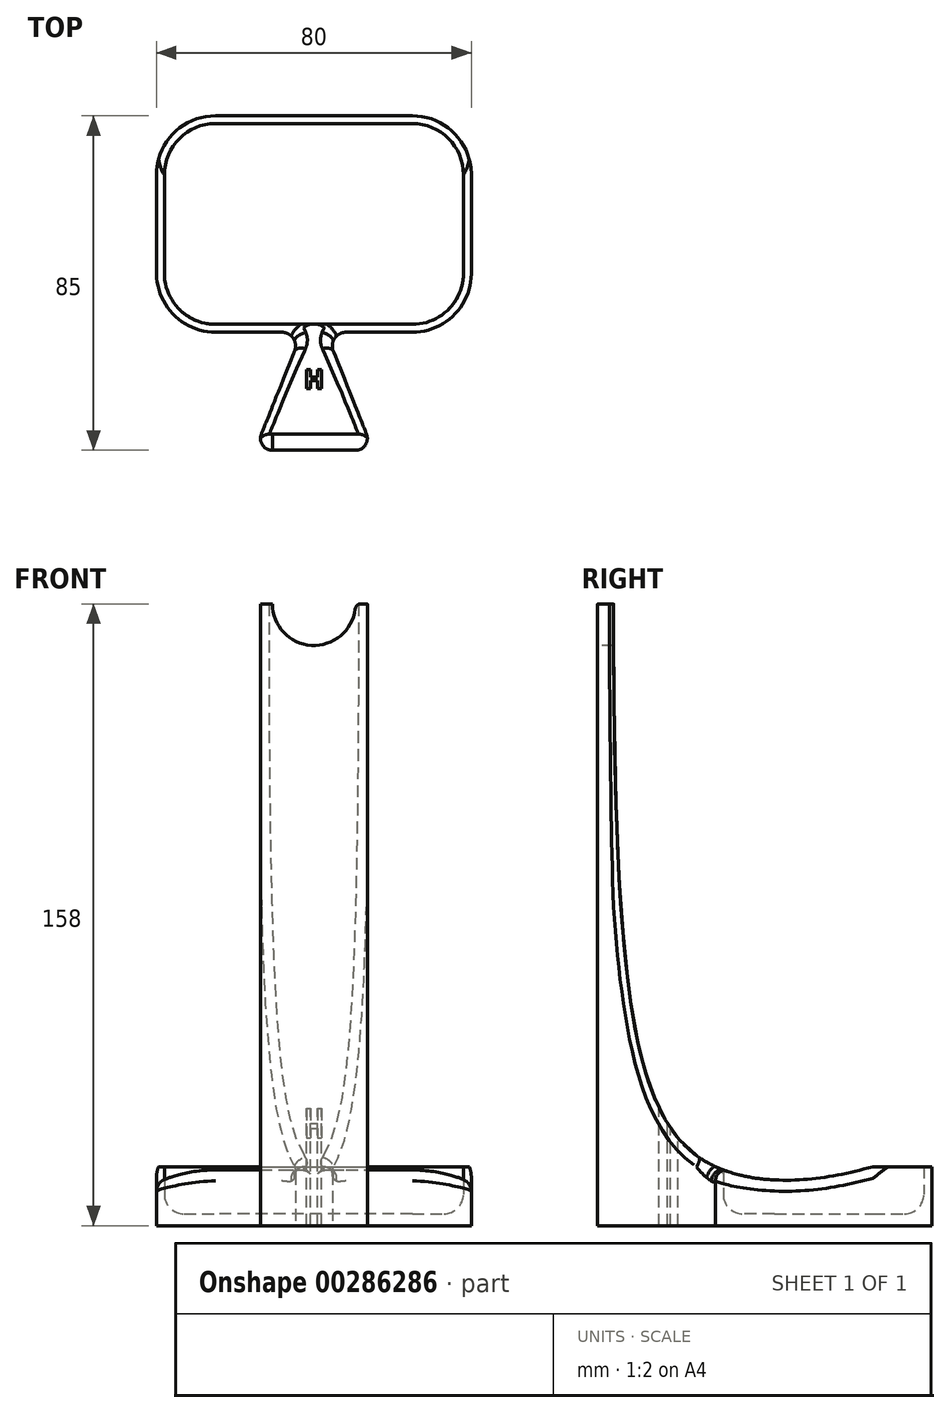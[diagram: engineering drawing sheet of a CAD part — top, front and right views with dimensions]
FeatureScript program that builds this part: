
annotation { "Feature Type Name" : "Feature", "Feature Type Description" : "" }
export const myFeature = defineFeature(function(context is Context, id is Id, definition is map)
    precondition{}
    {
        {
            var Q0;
            Q0=qCreatedBy(makeId("Top.planeOp"),FACE);
            var sketch = newSketch(context, id + "F0", { "sketchPlane" : qUnion([Q0])});
            skLineSegment(sketch, "E0.bottom", {"start": v(-25, 27.5) * mm, "end": v(25, 27.5) * mm});
            skLineSegment(sketch, "E0.top", {"start": v(-25, -27.5) * mm, "end": v(25, -27.5) * mm});
            skLineSegment(sketch, "E0.left", {"start": v(-40, 12.5) * mm, "end": v(-40, -12.5) * mm});
            skLineSegment(sketch, "E0.right", {"start": v(40, 12.5) * mm, "end": v(40, -12.5) * mm});
            skPoint(sketch, "E0.middle", {"position": v(0, 0) * mm});
            skPoint(sketch, "E1.visualSharp", {"position": v(-40, 27.5) * mm});
            skArc(sketch, "E1.filletArc", {"start": v(-25, 27.5) * mm, "mid": v(-35.6, 23.1) * mm, "end": v(-40, 12.5) * mm});
            skPoint(sketch, "E2.visualSharp", {"position": v(40, 27.5) * mm});
            skArc(sketch, "E2.filletArc", {"start": v(40, 12.5) * mm, "mid": v(35.6, 23.1) * mm, "end": v(25, 27.5) * mm});
            skPoint(sketch, "E3.visualSharp", {"position": v(40, -27.5) * mm});
            skArc(sketch, "E3.filletArc", {"start": v(25, -27.5) * mm, "mid": v(35.6, -23.1) * mm, "end": v(40, -12.5) * mm});
            skPoint(sketch, "E4.visualSharp", {"position": v(-40, -27.5) * mm});
            skArc(sketch, "E4.filletArc", {"start": v(-40, -12.5) * mm, "mid": v(-35.6, -23.1) * mm, "end": v(-25, -27.5) * mm});
            skArc(sketch, "E5.0", {"start": v(-25, 25.5) * mm, "mid": v(-34.2, 21.7) * mm, "end": v(-38, 12.5) * mm});
            skLineSegment(sketch, "E5.1", {"start": v(-38, 12.5) * mm, "end": v(-38, -12.5) * mm});
            skLineSegment(sketch, "E5.2", {"start": v(-25, 25.5) * mm, "end": v(25, 25.5) * mm});
            skArc(sketch, "E5.3", {"start": v(-38, -12.5) * mm, "mid": v(-34.2, -21.7) * mm, "end": v(-25, -25.5) * mm});
            skArc(sketch, "E5.4", {"start": v(38, 12.5) * mm, "mid": v(34.2, 21.7) * mm, "end": v(25, 25.5) * mm});
            skLineSegment(sketch, "E5.5", {"start": v(38, 12.5) * mm, "end": v(38, -12.5) * mm});
            skArc(sketch, "E5.6", {"start": v(25, -25.5) * mm, "mid": v(34.2, -21.7) * mm, "end": v(38, -12.5) * mm});
            skLineSegment(sketch, "E5.7", {"start": v(-25, -25.5) * mm, "end": v(25, -25.5) * mm});
            skLineSegment(sketch, "E6", {"start": v(-4.92, -32.3) * mm, "end": v(-13.35, -53.39) * mm});
            skLineSegment(sketch, "E7", {"start": v(-10.57, -57.5) * mm, "end": v(10.57, -57.5) * mm});
            skLineSegment(sketch, "E8", {"start": v(13.35, -53.39) * mm, "end": v(4.92, -32.3) * mm});
            skPoint(sketch, "E9", {"position": v(0, -57.5) * mm});
            skArc(sketch, "E10", {"start": v(-4.92, -32.3) * mm, "mid": v(-5.27, -29.04) * mm, "end": v(-8.17, -27.5) * mm});
            skArc(sketch, "E11.MirrorC", {"start": v(4.92, -32.3) * mm, "mid": v(5.27, -29.04) * mm, "end": v(8.17, -27.5) * mm});
            skPoint(sketch, "E12.orphan", {"position": v(3, -27.5) * mm});
            skPoint(sketch, "E13.orphan", {"position": v(-3, -27.5) * mm});
            skPoint(sketch, "E14.visualSharp", {"position": v(-15, -57.5) * mm});
            skArc(sketch, "E14.filletArc", {"start": v(-13.35, -53.39) * mm, "mid": v(-13.05, -56.18) * mm, "end": v(-10.57, -57.5) * mm});
            skPoint(sketch, "E15.visualSharp", {"position": v(15, -57.5) * mm});
            skArc(sketch, "E15.filletArc", {"start": v(10.57, -57.5) * mm, "mid": v(13.05, -56.18) * mm, "end": v(13.35, -53.39) * mm});
            skSolve(sketch);
        }
        {
            var Q0;
            Q0=makeQuery(id+"F0.imprint","IMPRINT",FACE,{"disambiguationData":[TD([[makeQuery(id+"F0.imprint","IMPRINT",EDGE,{"derivedFrom":sQuery(id+"F0.wireOp",EDGE,"E0.bottom")}),-1.0]])]});
            var Q1;
            Q1=makeQuery(id+"F0.imprint","IMPRINT",FACE,{"disambiguationData":[TD([[makeQuery(id+"F0.imprint","IMPRINT",EDGE,{"derivedFrom":sQuery(id+"F0.wireOp",EDGE,"E5.0")}),1.0]])]});
            var Q2;
            {var subQ0=sQuery(id+"F0.wireOp",EDGE,"E6");Q2=makeQuery(id+"F0.imprint","IMPRINT",FACE,{"disambiguationData":[TD([[makeQuery(id+"F0.imprint","IMPRINT",EDGE,{"derivedFrom":subQ0}),1.0]])]});}
            extrude(context, id + "F1", {"entities" : qUnion([Q0, Q1, Q2]), "depth" : 3 * mm});
        }
        {
            var Q0;
            Q0=makeQuery(id+"F0.imprint","IMPRINT",FACE,{"disambiguationData":[TD([[makeQuery(id+"F0.imprint","IMPRINT",EDGE,{"derivedFrom":sQuery(id+"F0.wireOp",EDGE,"E0.bottom")}),-1.0]])]});
            extrude(context, id + "F2", {"entities" : qUnion([Q0]), "operationType" : NewBodyOperationType.ADD, "depth" : 15 * mm});
        }
        {
            var Q0;
            {var subQ0=sQuery(id+"F0.wireOp",EDGE,"E7");var subQ1=sQuery(id+"F0.wireOp",EDGE,"E6");var subQ2=sQuery(id+"F0.wireOp",EDGE,"E3.filletArc");var subQ3=sQuery(id+"F0.wireOp",EDGE,"E0.top");var subQ4=sQuery(id+"F0.wireOp",EDGE,"E11.MirrorC");var subQ5=sQuery(id+"F0.wireOp",EDGE,"E4.filletArc");var subQ6=sQuery(id+"F0.wireOp",EDGE,"E10");var subQ7=sQuery(id+"F0.wireOp",EDGE,"E8");var subQ8=sQuery(id+"F0.wireOp",EDGE,"E14.filletArc");var subQ9=sQuery(id+"F0.wireOp",EDGE,"E15.filletArc");Q0=makeQuery(id+"F2.boolean.opBoolean","SPLIT",FACE,{"disambiguationData":[TD([makeQuery(id+"F1.opExtrude","SWEPT_FACE",FACE,{"disambiguationData":[OSD([subQ1])]})])],"derivedFrom":makeQuery(id+"F1.opExtrude","CAP_FACE",FACE,{"disambiguationData":[OSD([sQuery(id+"F0.wireOp",EDGE,"E0.bottom"),subQ3,sQuery(id+"F0.wireOp",EDGE,"E0.left"),sQuery(id+"F0.wireOp",EDGE,"E0.right"),sQuery(id+"F0.wireOp",EDGE,"E1.filletArc"),sQuery(id+"F0.wireOp",EDGE,"E2.filletArc"),subQ2,subQ5,subQ1,subQ0,subQ7,subQ6,subQ4,subQ8,subQ9])],"isStart":false})});}
            extrude(context, id + "F3", {"entities" : qUnion([Q0]), "operationType" : NewBodyOperationType.ADD, "depth" : 155 * mm});
        }
        {
            var Q0;
            Q0=qCreatedBy(makeId("Right.planeOp"),FACE);
            var sketch = newSketch(context, id + "F4", { "sketchPlane" : qUnion([Q0])});
            skLineSegment(sketch, "E16.0.0", {"start": v(-53.39, 0) * mm, "end": v(-57.5, 0) * mm});
            skLineSegment(sketch, "E16.0.1", {"start": v(-57.5, 0) * mm, "end": v(-57.5, 158) * mm});
            skLineSegment(sketch, "E16.0.2", {"start": v(-57.5, 158) * mm, "end": v(-53.39, 158) * mm});
            skLineSegment(sketch, "E16.0.3", {"start": v(-53.39, 158) * mm, "end": v(-53.39, 0) * mm});
            skLineSegment(sketch, "E16.1.0", {"start": v(-32.3, 0) * mm, "end": v(-53.39, 0) * mm});
            skLineSegment(sketch, "E16.1.1", {"start": v(-53.39, 0) * mm, "end": v(-53.39, 158) * mm});
            skLineSegment(sketch, "E16.1.2", {"start": v(-53.39, 158) * mm, "end": v(-32.3, 158) * mm});
            skLineSegment(sketch, "E16.1.3", {"start": v(-32.3, 17.8) * mm, "end": v(-32.3, 0) * mm});
            skLineSegment(sketch, "E16.2.0", {"start": v(-27.5, 0) * mm, "end": v(-32.3, 0) * mm});
            skLineSegment(sketch, "E16.2.1", {"start": v(-32.3, 0) * mm, "end": v(-32.3, 17.8) * mm});
            skLineSegment(sketch, "E16.2.2", {"start": v(-32.3, 158) * mm, "end": v(-27.5, 158) * mm});
            skLineSegment(sketch, "E16.2.3", {"start": v(-27.5, 158) * mm, "end": v(-27.5, 15) * mm});
            skLineSegment(sketch, "E16.2.4", {"start": v(-27.5, 15) * mm, "end": v(-27.5, 0) * mm});
            skLineSegment(sketch, "E16.3.0", {"start": v(-12.5, 0) * mm, "end": v(-27.5, 0) * mm});
            skLineSegment(sketch, "E16.3.1", {"start": v(-27.5, 0) * mm, "end": v(-27.5, 15) * mm});
            skLineSegment(sketch, "E16.3.2", {"start": v(-27.5, 15) * mm, "end": v(-12.5, 15) * mm});
            skLineSegment(sketch, "E16.3.3", {"start": v(-12.5, 11.62) * mm, "end": v(-12.5, 0) * mm});
            skLineSegment(sketch, "E16.4.0", {"start": v(12.5, 0) * mm, "end": v(-12.5, 0) * mm});
            skLineSegment(sketch, "E16.4.1", {"start": v(-12.5, 0) * mm, "end": v(-12.5, 11.62) * mm});
            skLineSegment(sketch, "E16.4.2", {"start": v(-12.5, 15) * mm, "end": v(12.5, 15) * mm});
            skLineSegment(sketch, "E16.4.3", {"start": v(12.5, 15) * mm, "end": v(12.5, 0) * mm});
            skLineSegment(sketch, "E16.5.0", {"start": v(27.5, 0) * mm, "end": v(12.5, 0) * mm});
            skLineSegment(sketch, "E16.5.1", {"start": v(12.5, 0) * mm, "end": v(12.5, 15) * mm});
            skLineSegment(sketch, "E16.5.2", {"start": v(12.5, 15) * mm, "end": v(27.5, 15) * mm});
            skLineSegment(sketch, "E16.5.3", {"start": v(27.5, 15) * mm, "end": v(27.5, 0) * mm});
            skFitSpline(sketch, "E17", {"points": [v(-53.39, 158) * mm, v(-27.5, 15) * mm, v(12.5, 15) * mm], "startDerivative": vector(0, -478.35) * mm, "endDerivative": vector(129.4, 37.5) * mm});
            skSolve(sketch);
        }
        {
            var Q0;
            {var subQ2=sQuery(id+"F4.wireOp",EDGE,"E16.1.2");Q0=makeQuery(id+"F4.imprint","IMPRINT",FACE,{"disambiguationData":[TD([[makeQuery(id+"F4.imprint","IMPRINT",EDGE,{"derivedFrom":subQ2}),-1.0]])]});}
            var Q1;
            {var subQ0=sQuery(id+"F4.wireOp",EDGE,"E16.3.2");Q1=makeQuery(id+"F4.imprint","IMPRINT",FACE,{"disambiguationData":[TD([[makeQuery(id+"F4.imprint","IMPRINT",EDGE,{"derivedFrom":subQ0}),-1.0]])]});}
            extrude(context, id + "F5", {"entities" : qUnion([Q0, Q1]), "operationType" : NewBodyOperationType.REMOVE, "endBound" : BoundingType.SYMMETRIC, "oppositeDirection" : true, "depth" : 150 * mm});
        }
        {
            var Q0;
            {var subQ0=sQuery(id+"F0.wireOp",EDGE,"E7");Q0=makeQuery(id+"F3.boolean.opBoolean","MERGE",FACE,{"derivedFrom":[makeQuery(id+"F1.opExtrude","SWEPT_FACE",FACE,{"disambiguationData":[OSD([subQ0])]}),makeQuery(id+"F3.opExtrude","SWEPT_FACE",FACE,{"disambiguationData":[OSD([subQ0])]})]});}
            var sketch = newSketch(context, id + "F6", { "sketchPlane" : qUnion([Q0])});
            skLineSegment(sketch, "E18.0.0", {"start": v(-13.57, 0) * mm, "end": v(-10.57, 0) * mm});
            skLineSegment(sketch, "E18.0.1", {"start": v(-10.57, 0) * mm, "end": v(-10.57, 158) * mm});
            skLineSegment(sketch, "E18.0.2", {"start": v(-10.57, 158) * mm, "end": v(-13.57, 158) * mm});
            skLineSegment(sketch, "E18.0.3", {"start": v(-13.35, 158) * mm, "end": v(-13.35, 0) * mm});
            skLineSegment(sketch, "E18.2.0", {"start": v(10.57, 0) * mm, "end": v(13.57, 0) * mm});
            skLineSegment(sketch, "E18.2.1", {"start": v(13.35, 0) * mm, "end": v(13.35, 158) * mm});
            skLineSegment(sketch, "E18.2.2", {"start": v(13.57, 158) * mm, "end": v(10.57, 158) * mm});
            skLineSegment(sketch, "E18.2.3", {"start": v(10.57, 158) * mm, "end": v(10.57, 0) * mm});
            skArc(sketch, "E19", {"start": v(-10.57, 158) * mm, "mid": v(0, 147.43) * mm, "end": v(10.57, 158) * mm});
            skSolve(sketch);
        }
        {
            var Q0;
            {var subQ1=makeQuery(id+"F3.opExtrude","CAP_EDGE",EDGE,{"disambiguationData":[OSD([sQuery(id+"F0.wireOp",EDGE,"E7")])],"isStart":false});Q0=makeQuery(id+"F6.imprint","IMPRINT",FACE,{"disambiguationData":[TD([[makeQuery(id+"F6.imprint","IMPRINT",EDGE,{"derivedFrom":subQ1}),-1.0]])]});}
            extrude(context, id + "F7", {"entities" : qUnion([Q0]), "operationType" : NewBodyOperationType.REMOVE, "oppositeDirection" : true, "depth" : 25 * mm});
        }
        {
            var Q0;
            Q0=makeQuery(id+"F7.boolean.opBoolean","COPY",EDGE,{"derivedFrom":makeQuery(id+"F7.opExtrude","SWEPT_EDGE",EDGE,{"disambiguationData":[OSD([sQuery(id+"F0.wireOp",EDGE,"E7"),sQuery(id+"F6.wireOp",EDGE,"E18.0.1"),sQuery(id+"F6.wireOp",EDGE,"E18.0.2"),sQuery(id+"F6.wireOp",EDGE,"E19")])]})});
            var Q1;
            Q1=makeQuery(id+"F7.boolean.opBoolean","COPY",EDGE,{"derivedFrom":makeQuery(id+"F7.opExtrude","SWEPT_EDGE",EDGE,{"disambiguationData":[OSD([sQuery(id+"F0.wireOp",EDGE,"E7"),sQuery(id+"F6.wireOp",EDGE,"E18.2.2"),sQuery(id+"F6.wireOp",EDGE,"E18.2.3"),sQuery(id+"F6.wireOp",EDGE,"E19")])]})});
            fillet(context, id + "F8", {"entities" : qUnion([Q0, Q1]), "radius" : 1.5 * mm, "tangentPropagation" : true, "allowEdgeOverflow" : false});
        }
        {
            var Q0;
            {var subQ0=sQuery(id+"F4.wireOp",EDGE,"E17");var subQ1=makeQuery(id+"F4.imprint","INTERSECT",VERTEX,{"derivedFrom":[sQuery(id+"F4.wireOp",EDGE,"E16.2.1"),subQ0]});var subQ2=sQuery(id+"F0.wireOp",EDGE,"E6");Q0=makeQuery(id+"F5.boolean.opBoolean","INTERSECT",EDGE,{"derivedFrom":[makeQuery(id+"F3.boolean.opBoolean","MERGE",FACE,{"derivedFrom":[makeQuery(id+"F1.opExtrude","SWEPT_FACE",FACE,{"disambiguationData":[OSD([subQ2])]}),makeQuery(id+"F3.opExtrude","SWEPT_FACE",FACE,{"disambiguationData":[OSD([subQ2])]})]}),makeQuery(id+"F5.opExtrude","SWEPT_FACE",FACE,{"disambiguationData":[OSD([subQ0]),TDD([makeQuery(id+"F4.imprint","IMPRINT",EDGE,{"disambiguationData":[TD([[subQ1,1.0]])],"derivedFrom":subQ0}),makeQuery(id+"F4.imprint","IMPRINT",EDGE,{"disambiguationData":[TD([[subQ1,-1.0]])],"derivedFrom":subQ0})])]})]});}
            var Q1;
            {var subQ0=sQuery(id+"F4.wireOp",EDGE,"E17");var subQ1=makeQuery(id+"F4.imprint","INTERSECT",VERTEX,{"derivedFrom":[sQuery(id+"F4.wireOp",EDGE,"E16.2.1"),subQ0]});var subQ2=sQuery(id+"F0.wireOp",EDGE,"E8");Q1=makeQuery(id+"F5.boolean.opBoolean","INTERSECT",EDGE,{"derivedFrom":[makeQuery(id+"F3.boolean.opBoolean","MERGE",FACE,{"derivedFrom":[makeQuery(id+"F1.opExtrude","SWEPT_FACE",FACE,{"disambiguationData":[OSD([subQ2])]}),makeQuery(id+"F3.opExtrude","SWEPT_FACE",FACE,{"disambiguationData":[OSD([subQ2])]})]}),makeQuery(id+"F5.opExtrude","SWEPT_FACE",FACE,{"disambiguationData":[OSD([subQ0]),TDD([makeQuery(id+"F4.imprint","IMPRINT",EDGE,{"disambiguationData":[TD([[subQ1,1.0]])],"derivedFrom":subQ0}),makeQuery(id+"F4.imprint","IMPRINT",EDGE,{"disambiguationData":[TD([[subQ1,-1.0]])],"derivedFrom":subQ0})])]})]});}
            fillet(context, id + "F9", {"entities" : qUnion([Q0, Q1]), "radius" : 3 * mm, "tangentPropagation" : true, "allowEdgeOverflow" : false});
        }
        {
            var Q0;
            Q0=makeQuery(id+"F2.boolean.opBoolean","SPLIT",FACE,{"disambiguationData":[TD([makeQuery(id+"F2.opExtrude","SWEPT_FACE",FACE,{"disambiguationData":[OSD([sQuery(id+"F0.wireOp",EDGE,"E5.0")])]})])],"derivedFrom":makeQuery(id+"F1.opExtrude","CAP_FACE",FACE,{"disambiguationData":[OSD([sQuery(id+"F0.wireOp",EDGE,"E0.bottom"),sQuery(id+"F0.wireOp",EDGE,"E0.top"),sQuery(id+"F0.wireOp",EDGE,"E0.left"),sQuery(id+"F0.wireOp",EDGE,"E0.right"),sQuery(id+"F0.wireOp",EDGE,"E1.filletArc"),sQuery(id+"F0.wireOp",EDGE,"E2.filletArc"),sQuery(id+"F0.wireOp",EDGE,"E3.filletArc"),sQuery(id+"F0.wireOp",EDGE,"E4.filletArc"),sQuery(id+"F0.wireOp",EDGE,"E6"),sQuery(id+"F0.wireOp",EDGE,"E7"),sQuery(id+"F0.wireOp",EDGE,"E8"),sQuery(id+"F0.wireOp",EDGE,"E10"),sQuery(id+"F0.wireOp",EDGE,"E11.MirrorC"),sQuery(id+"F0.wireOp",EDGE,"E14.filletArc"),sQuery(id+"F0.wireOp",EDGE,"E15.filletArc")])],"isStart":false})});
            var sketch = newSketch(context, id + "F10", { "sketchPlane" : qUnion([Q0])});
            skLineSegment(sketch, "E20.0.0", {"start": v(3.42, -25.5) * mm, "end": v(-3.42, -25.5) * mm});
            skFitSpline(sketch, "E20.0.1", {"points": [v(-3.42, -25.5) * mm, v(-3.2, -25.71) * mm, v(-2.9, -26.05) * mm, v(-2.57, -26.53) * mm, v(-2.26, -27.04) * mm, v(-1.97, -27.7) * mm, v(-1.74, -28.52) * mm, v(-1.65, -29.36) * mm, v(-1.69, -30.17) * mm, v(-1.84, -30.96) * mm, v(-2.03, -31.46) * mm, v(-2.13, -31.7) * mm]});
            skFitSpline(sketch, "E20.0.2", {"points": [v(-2.13, -31.7) * mm, v(-2.67, -32.91) * mm, v(-3.42, -34.6) * mm, v(-4.32, -36.62) * mm, v(-4.94, -38.02) * mm, v(-5.5, -39.32) * mm, v(-6, -40.48) * mm, v(-6.46, -41.54) * mm, v(-7, -42.81) * mm, v(-7.46, -43.91) * mm, v(-7.86, -44.88) * mm, v(-8.23, -45.75) * mm, v(-8.62, -46.7) * mm, v(-9.14, -47.97) * mm, v(-9.64, -49.2) * mm, v(-10.08, -50.3) * mm, v(-10.42, -51.13) * mm, v(-10.76, -51.98) * mm, v(-11.03, -52.66) * mm, v(-11.22, -53.12) * mm, v(-11.3, -53.35) * mm, v(-11.32, -53.39) * mm, v(-11.32, -53.39) * mm]});
            skFitSpline(sketch, "E20.0.3", {"points": [v(-11.32, -53.39) * mm, v(-11.1, -53.39) * mm, v(-10.7, -53.39) * mm, v(-10.52, -53.39) * mm, v(-10.49, -53.39) * mm]});
            skFitSpline(sketch, "E20.0.4", {"points": [v(-10.49, -53.39) * mm, v(-10.4, -53.39) * mm, v(-10.2, -53.38) * mm, v(-9.76, -53.38) * mm, v(-9.36, -53.38) * mm, v(-8.88, -53.38) * mm, v(-8.32, -53.38) * mm, v(-7.69, -53.38) * mm, v(-7, -53.37) * mm, v(-6.26, -53.37) * mm, v(-5.46, -53.37) * mm, v(-4.62, -53.37) * mm, v(-3.75, -53.37) * mm, v(-2.84, -53.37) * mm, v(-1.9, -53.37) * mm, v(-0.95, -53.37) * mm, v(0, -53.36) * mm, v(0.95, -53.37) * mm, v(2.23, -53.37) * mm, v(3.75, -53.37) * mm, v(5.5, -53.37) * mm, v(6.77, -53.37) * mm, v(7.7, -53.38) * mm, v(8.32, -53.38) * mm, v(8.87, -53.38) * mm, v(9.36, -53.38) * mm, v(9.77, -53.38) * mm, v(10.2, -53.38) * mm, v(10.4, -53.39) * mm, v(10.49, -53.39) * mm]});
            skFitSpline(sketch, "E20.0.5", {"points": [v(10.49, -53.39) * mm, v(10.52, -53.39) * mm, v(10.7, -53.39) * mm, v(11.1, -53.39) * mm, v(11.32, -53.39) * mm]});
            skFitSpline(sketch, "E20.0.6", {"points": [v(11.32, -53.39) * mm, v(11.32, -53.39) * mm, v(11.3, -53.35) * mm, v(11.22, -53.13) * mm, v(11.03, -52.66) * mm, v(10.76, -51.98) * mm, v(10.42, -51.13) * mm, v(10.08, -50.3) * mm, v(9.64, -49.2) * mm, v(9.14, -47.97) * mm, v(8.62, -46.7) * mm, v(8.23, -45.75) * mm, v(7.87, -44.88) * mm, v(7.46, -43.91) * mm, v(7, -42.81) * mm, v(6.46, -41.54) * mm, v(6, -40.48) * mm, v(5.5, -39.32) * mm, v(4.94, -38.02) * mm, v(4.32, -36.62) * mm, v(3.42, -34.6) * mm, v(2.67, -32.91) * mm, v(2.13, -31.7) * mm]});
            skFitSpline(sketch, "E20.0.7", {"points": [v(2.13, -31.7) * mm, v(1.92, -31.22) * mm, v(1.7, -30.46) * mm, v(1.65, -29.36) * mm, v(1.73, -28.67) * mm, v(1.85, -28.12) * mm, v(2.03, -27.58) * mm, v(2.32, -26.91) * mm, v(2.72, -26.3) * mm, v(3.1, -25.82) * mm, v(3.3, -25.6) * mm, v(3.42, -25.5) * mm]});
            skText(sketch, "E21", { "text": "H", "fontName": "OpenSans-Bold.ttf"});
            skLineSegment(sketch, "E22", {"start": v(2.13, -31.7) * mm, "end": v(2.13, -53.37) * mm, "construction": true});
            skLineSegment(sketch, "E23", {"start": v(-2.13, -31.7) * mm, "end": v(-2.13, -53.37) * mm, "construction": true});
            const initialGuessF10  = {"E21": [-0.00251, -0.04178, 1, 0, 0.00477]};
            skSetInitialGuess(sketch, initialGuessF10);
            skSolve(sketch);
        }
        {
            var Q0;
            Q0=makeQuery(id+"F10.imprint","IMPRINT",FACE,{"disambiguationData":[TD([[makeQuery(id+"F10.imprint","IMPRINT",EDGE,{"derivedFrom":sQuery(id+"F10.wireOp",EDGE,"E21.sketch_text.stroke-0")}),-1.0]])]});
            extrude(context, id + "F11", {"entities" : qUnion([Q0]), "operationType" : NewBodyOperationType.REMOVE, "endBound" : BoundingType.SYMMETRIC, "oppositeDirection" : true, "depth" : 100 * mm});
        }
        {
            var Q0;
            Q0=makeQuery(id+"F2.boolean.opBoolean","INTERSECT",EDGE,{"derivedFrom":[makeQuery(id+"F1.opExtrude","CAP_FACE",FACE,{"disambiguationData":[OSD([sQuery(id+"F0.wireOp",EDGE,"E0.bottom"),sQuery(id+"F0.wireOp",EDGE,"E0.top"),sQuery(id+"F0.wireOp",EDGE,"E0.left"),sQuery(id+"F0.wireOp",EDGE,"E0.right"),sQuery(id+"F0.wireOp",EDGE,"E1.filletArc"),sQuery(id+"F0.wireOp",EDGE,"E2.filletArc"),sQuery(id+"F0.wireOp",EDGE,"E3.filletArc"),sQuery(id+"F0.wireOp",EDGE,"E4.filletArc"),sQuery(id+"F0.wireOp",EDGE,"E6"),sQuery(id+"F0.wireOp",EDGE,"E7"),sQuery(id+"F0.wireOp",EDGE,"E8"),sQuery(id+"F0.wireOp",EDGE,"E10"),sQuery(id+"F0.wireOp",EDGE,"E11.MirrorC"),sQuery(id+"F0.wireOp",EDGE,"E14.filletArc"),sQuery(id+"F0.wireOp",EDGE,"E15.filletArc")])],"isStart":false}),makeQuery(id+"F2.opExtrude","SWEPT_FACE",FACE,{"disambiguationData":[OSD([sQuery(id+"F0.wireOp",EDGE,"E5.3")])]})]});
            fillet(context, id + "F12", {"entities" : qUnion([Q0]), "radius" : 5 * mm, "tangentPropagation" : true, "allowEdgeOverflow" : false});
        }
        {
            var Q0;
            {var subQ0=sQuery(id+"F4.wireOp",EDGE,"E17");var subQ1=makeQuery(id+"F4.imprint","INTERSECT",VERTEX,{"derivedFrom":[sQuery(id+"F4.wireOp",EDGE,"E16.4.1"),subQ0]});var subQ3=makeQuery(id+"F4.imprint","INTERSECT",VERTEX,{"derivedFrom":[sQuery(id+"F4.wireOp",EDGE,"E16.2.1"),subQ0]});Q0=makeQuery(id+"F5.boolean.opBoolean","INTERSECT",EDGE,{"derivedFrom":[makeQuery(id+"F2.opExtrude","SWEPT_FACE",FACE,{"disambiguationData":[OSD([sQuery(id+"F0.wireOp",EDGE,"E5.7")])]}),makeQuery(id+"F5.opExtrude","SWEPT_FACE",FACE,{"disambiguationData":[OSD([subQ0]),TDD([makeQuery(id+"F4.imprint","IMPRINT",EDGE,{"disambiguationData":[TD([[subQ3,1.0]])],"derivedFrom":subQ0}),makeQuery(id+"F4.imprint","IMPRINT",EDGE,{"disambiguationData":[TD([[subQ3,-1.0]])],"derivedFrom":subQ0})])]}),makeQuery(id+"F5.opExtrude","SWEPT_FACE",FACE,{"disambiguationData":[OSD([subQ0]),TDD([makeQuery(id+"F4.imprint","IMPRINT",EDGE,{"disambiguationData":[TD([[subQ1,1.0]])],"derivedFrom":subQ0}),makeQuery(id+"F4.imprint","IMPRINT",EDGE,{"disambiguationData":[TD([[subQ1,-1.0]])],"derivedFrom":subQ0})])]})]});}
            fillet(context, id + "F13", {"entities" : qUnion([Q0]), "radius" : 1.5 * mm, "allowEdgeOverflow" : false});
        }
    });
